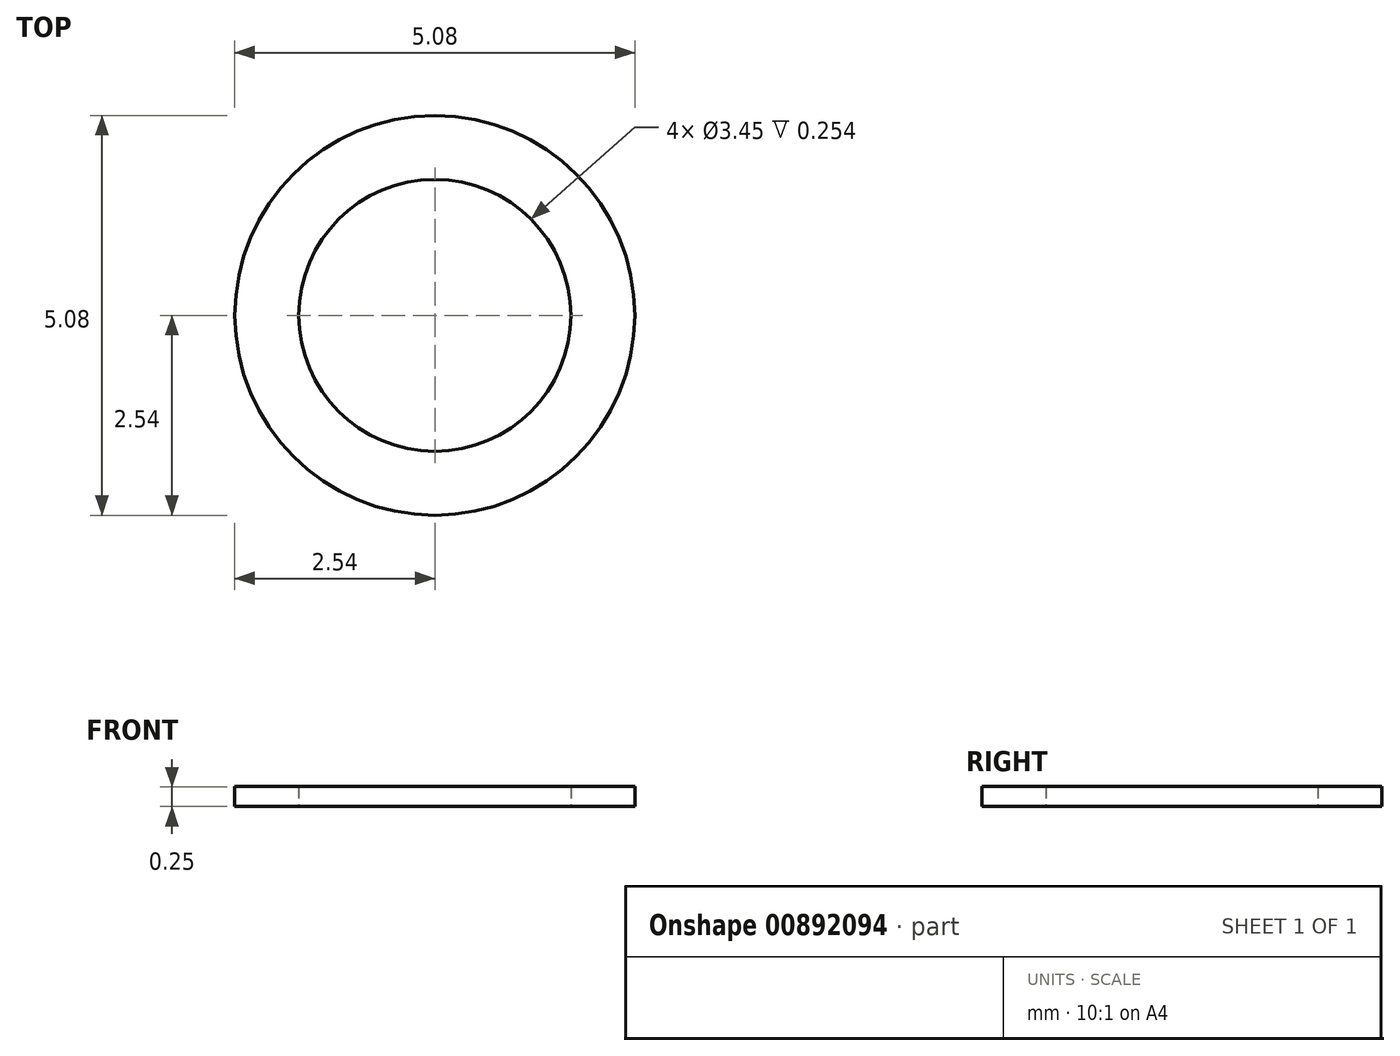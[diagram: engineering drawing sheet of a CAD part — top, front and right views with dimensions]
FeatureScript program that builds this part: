
annotation { "Feature Type Name" : "Feature", "Feature Type Description" : "" }
export const myFeature = defineFeature(function(context is Context, id is Id, definition is map)
    precondition{}
    {
        {
            var Q0;
            Q0=qCreatedBy(makeId("Top.planeOp"),FACE);
            var sketch = newSketch(context, id + "F0", { "sketchPlane" : qUnion([Q0])});
            skCircle(sketch, "E0", {"center": v(0, 0) * mm, "radius": 1.73 * mm});
            skCircle(sketch, "E1", {"center": v(0, 0) * mm, "radius": 2.54 * mm});
            skSolve(sketch);
        }
        {
            var Q0;
            Q0=makeQuery(id+"F0.imprint","IMPRINT",FACE,{"disambiguationData":[TD([[makeQuery(id+"F0.imprint","IMPRINT",EDGE,{"derivedFrom":sQuery(id+"F0.wireOp",EDGE,"E0")}),-1.0]])]});
            extrude(context, id + "F1", {"entities" : qUnion([Q0]), "depth" : 0.25 * mm, "offsetDistance" : 25.4 * mm});
        }
    });
